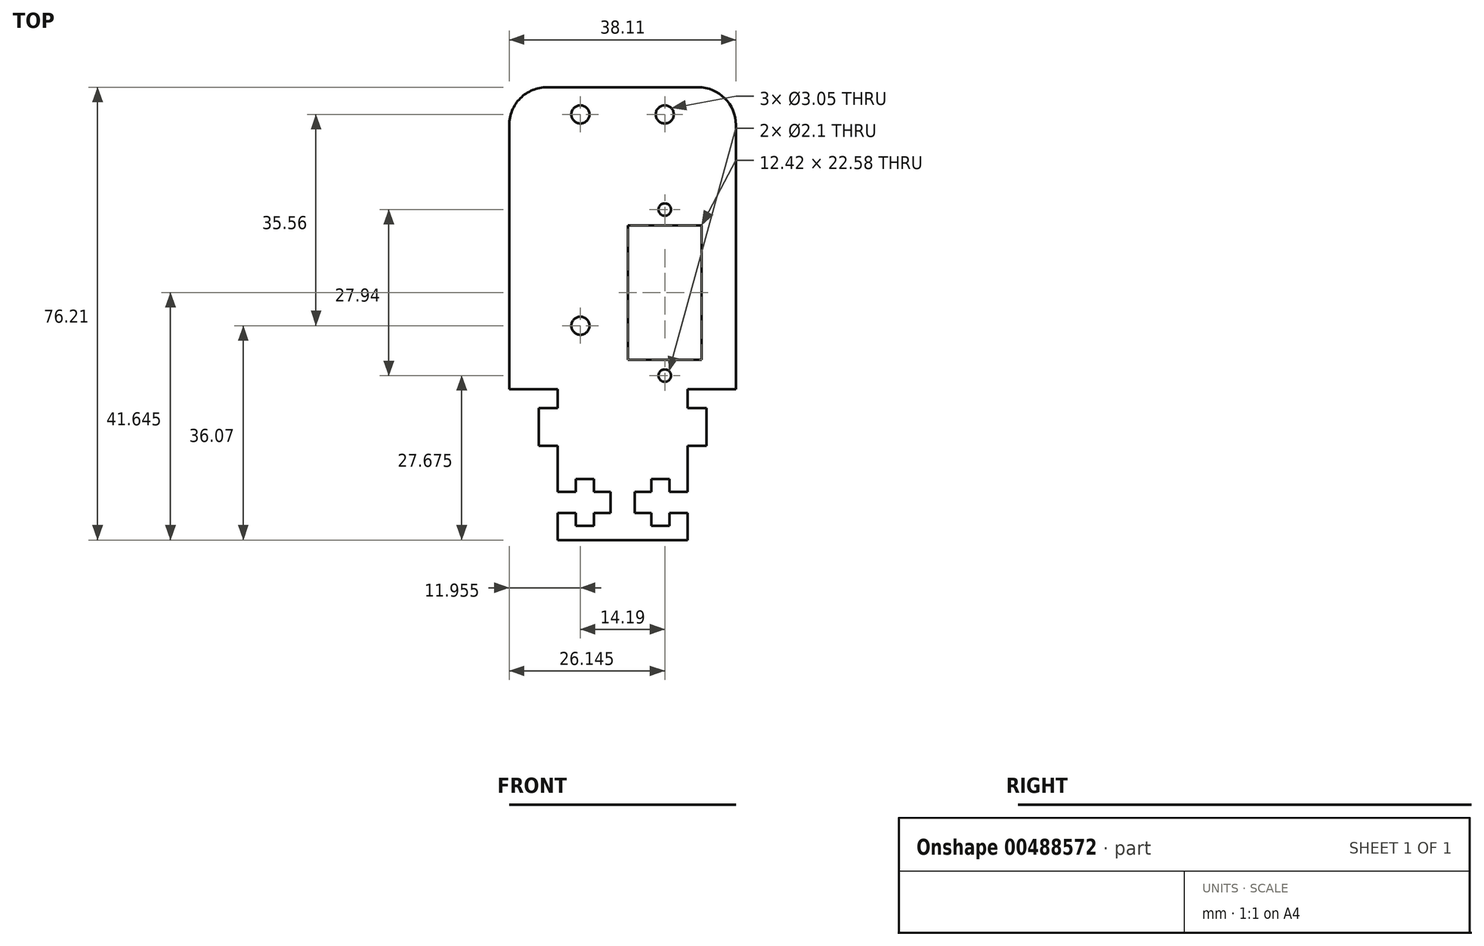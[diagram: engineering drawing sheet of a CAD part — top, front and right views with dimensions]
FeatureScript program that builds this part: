
annotation { "Feature Type Name" : "Feature", "Feature Type Description" : "" }
export const myFeature = defineFeature(function(context is Context, id is Id, definition is map)
    precondition{}
    {
        {
            var Q0;
            Q0=qCreatedBy(makeId("Top.planeOp"),FACE);
            var sketch = newSketch(context, id + "F0", { "sketchPlane" : qUnion([Q0])});
            skLineSegment(sketch, "E0.bottom", {"start": v(12.7, 41.7) * mm, "end": v(-12.7, 41.7) * mm});
            skLineSegment(sketch, "E0.left", {"start": v(19.05, 35.36) * mm, "end": v(19.06, -9.1) * mm});
            skLineSegment(sketch, "E0.right", {"start": v(-19.05, 35.35) * mm, "end": v(-19.04, -9.1) * mm});
            skPoint(sketch, "E0.middle", {"position": v(0, 0) * mm});
            skLineSegment(sketch, "E1.bottom", {"start": v(0.88, -4.14) * mm, "end": v(13.3, -4.14) * mm});
            skLineSegment(sketch, "E1.top", {"start": v(0.88, 18.44) * mm, "end": v(13.3, 18.44) * mm});
            skLineSegment(sketch, "E1.left", {"start": v(0.88, -4.14) * mm, "end": v(0.88, 18.44) * mm});
            skLineSegment(sketch, "E1.right", {"start": v(13.3, -4.14) * mm, "end": v(13.3, 18.44) * mm});
            skCircle(sketch, "E2", {"center": v(7.1, 1.57) * mm, "radius": 4.47 * mm, "construction": true});
            skPoint(sketch, "E2.centerSnap0", {"position": v(7.1, -4.14) * mm});
            skCircle(sketch, "E3", {"center": v(7.1, 6.04) * mm, "radius": 1.76 * mm, "construction": true});
            skCircle(sketch, "E4", {"center": v(-7.1, 1.57) * mm, "radius": 1.52 * mm});
            skLineSegment(sketch, "E5.bottom", {"start": v(13.3, 23.26) * mm, "end": v(1.1, 23.26) * mm, "construction": true});
            skLineSegment(sketch, "E5.top", {"start": v(13.3, -8.97) * mm, "end": v(1.1, -8.97) * mm, "construction": true});
            skLineSegment(sketch, "E5.left", {"start": v(13.3, 23.26) * mm, "end": v(13.3, -8.97) * mm, "construction": true});
            skLineSegment(sketch, "E5.right", {"start": v(1.1, 23.26) * mm, "end": v(1.1, -8.97) * mm, "construction": true});
            skPoint(sketch, "E5.middle.positionSnap0", {"position": v(0, 7.03) * mm});
            skPoint(sketch, "E5.middle.positionSnap1", {"position": v(7.1, 18.44) * mm});
            skPoint(sketch, "E5.centerSnap0", {"position": v(0.88, 7.15) * mm});
            skPoint(sketch, "E5.centerSnap1", {"position": v(7.1, 18.44) * mm});
            skCircle(sketch, "E6", {"center": v(7.1, 37.13) * mm, "radius": 1.52 * mm});
            skCircle(sketch, "E7", {"center": v(7.1, -6.82) * mm, "radius": 1.05 * mm});
            skCircle(sketch, "E8", {"center": v(-7.1, 37.13) * mm, "radius": 1.52 * mm});
            skPoint(sketch, "E9.visualSharp", {"position": v(-19.05, 41.7) * mm});
            skArc(sketch, "E9.filletArc", {"start": v(-12.7, 41.7) * mm, "mid": v(-17.2, 39.84) * mm, "end": v(-19.05, 35.35) * mm});
            skPoint(sketch, "E10.visualSharp", {"position": v(19.05, 41.7) * mm});
            skArc(sketch, "E10.filletArc", {"start": v(19.05, 35.36) * mm, "mid": v(17.19, 39.85) * mm, "end": v(12.7, 41.7) * mm});
            skCircle(sketch, "E11", {"center": v(7.1, 21.12) * mm, "radius": 1.05 * mm});
            skLineSegment(sketch, "E12", {"start": v(-7.1, 1.57) * mm, "end": v(0, 1.57) * mm, "construction": true});
            skLineSegment(sketch, "E13", {"start": v(0, 1.57) * mm, "end": v(7.1, 1.57) * mm, "construction": true});
            skLineSegment(sketch, "E14", {"start": v(-19.04, -9.1) * mm, "end": v(-10.9, -9.1) * mm});
            skLineSegment(sketch, "E15", {"start": v(-10.9, -9.1) * mm, "end": v(-10.9, -12.27) * mm});
            skLineSegment(sketch, "E16", {"start": v(-10.9, -34.5) * mm, "end": v(10.92, -34.5) * mm});
            skLineSegment(sketch, "E17", {"start": v(10.92, -34.5) * mm, "end": v(10.92, -29.93) * mm});
            skLineSegment(sketch, "E18", {"start": v(10.92, -9.1) * mm, "end": v(19.06, -9.1) * mm});
            skLineSegment(sketch, "E19.right", {"start": v(-14.07, -12.27) * mm, "end": v(-14.07, -18.62) * mm});
            skLineSegment(sketch, "E20", {"start": v(-14.07, -12.27) * mm, "end": v(-10.9, -12.27) * mm});
            skLineSegment(sketch, "E21", {"start": v(-14.07, -18.62) * mm, "end": v(-10.9, -18.62) * mm});
            skLineSegment(sketch, "E22", {"start": v(10.92, -12.27) * mm, "end": v(14.1, -12.27) * mm});
            skLineSegment(sketch, "E23", {"start": v(14.1, -12.27) * mm, "end": v(14.1, -18.62) * mm});
            skLineSegment(sketch, "E24", {"start": v(14.1, -18.62) * mm, "end": v(10.92, -18.62) * mm});
            skLineSegment(sketch, "E25.trimOffspring", {"start": v(10.92, -12.27) * mm, "end": v(10.92, -9.1) * mm});
            skLineSegment(sketch, "E26.trimOffspring", {"start": v(-10.9, -18.62) * mm, "end": v(-10.9, -26.37) * mm});
            skLineSegment(sketch, "E27.bottom", {"start": v(10.92, -26.37) * mm, "end": v(7.85, -26.37) * mm});
            skLineSegment(sketch, "E27.top", {"start": v(10.92, -29.93) * mm, "end": v(7.85, -29.93) * mm});
            skLineSegment(sketch, "E27.right", {"start": v(2.03, -26.37) * mm, "end": v(2.03, -29.93) * mm});
            skLineSegment(sketch, "E28.bottom", {"start": v(7.85, -32.08) * mm, "end": v(4.8, -32.08) * mm});
            skLineSegment(sketch, "E28.top", {"start": v(7.85, -24.21) * mm, "end": v(4.8, -24.21) * mm});
            skLineSegment(sketch, "E28.left", {"start": v(7.85, -32.08) * mm, "end": v(7.85, -29.93) * mm});
            skLineSegment(sketch, "E28.right", {"start": v(4.8, -32.08) * mm, "end": v(4.8, -29.93) * mm});
            skPoint(sketch, "E28.middle", {"position": v(6.33, -28.15) * mm});
            skPoint(sketch, "E28.middle.positionSnap0", {"position": v(10.92, -28.15) * mm});
            skPoint(sketch, "E28.centerSnap0", {"position": v(10.92, -28.15) * mm});
            skLineSegment(sketch, "E29.trimOffspring", {"start": v(4.8, -26.37) * mm, "end": v(2.03, -26.37) * mm});
            skLineSegment(sketch, "E30.trimOffspring", {"start": v(4.8, -26.37) * mm, "end": v(4.8, -24.21) * mm});
            skLineSegment(sketch, "E31.trimOffspring", {"start": v(7.85, -26.37) * mm, "end": v(7.85, -24.21) * mm});
            skLineSegment(sketch, "E32.trimOffspring", {"start": v(4.8, -29.93) * mm, "end": v(2.03, -29.93) * mm});
            skLineSegment(sketch, "E33.trimOffspring", {"start": v(10.92, -26.37) * mm, "end": v(10.92, -18.62) * mm});
            skLineSegment(sketch, "E34.MirrorCS", {"start": v(-10.92, -26.37) * mm, "end": v(-7.85, -26.37) * mm});
            skLineSegment(sketch, "E35.MirrorCS", {"start": v(-10.92, -29.93) * mm, "end": v(-7.85, -29.93) * mm});
            skLineSegment(sketch, "E36.MirrorCS", {"start": v(-7.85, -32.08) * mm, "end": v(-4.8, -32.08) * mm});
            skLineSegment(sketch, "E37.MirrorCS", {"start": v(-7.85, -32.08) * mm, "end": v(-7.85, -29.93) * mm});
            skLineSegment(sketch, "E38.MirrorCS", {"start": v(-4.8, -32.08) * mm, "end": v(-4.8, -29.93) * mm});
            skLineSegment(sketch, "E39.MirrorCS", {"start": v(-4.8, -29.93) * mm, "end": v(-2.03, -29.93) * mm});
            skLineSegment(sketch, "E40.MirrorCS", {"start": v(-2.03, -26.37) * mm, "end": v(-2.03, -29.93) * mm});
            skLineSegment(sketch, "E41.MirrorCS", {"start": v(-4.8, -26.37) * mm, "end": v(-2.03, -26.37) * mm});
            skLineSegment(sketch, "E42.MirrorCS", {"start": v(-4.8, -26.37) * mm, "end": v(-4.8, -24.21) * mm});
            skLineSegment(sketch, "E43.MirrorCS", {"start": v(-7.85, -24.21) * mm, "end": v(-4.8, -24.21) * mm});
            skLineSegment(sketch, "E44.MirrorCS", {"start": v(-7.85, -26.37) * mm, "end": v(-7.85, -24.21) * mm});
            skLineSegment(sketch, "E45.trimOffspring", {"start": v(-10.9, -29.93) * mm, "end": v(-10.9, -34.5) * mm});
            skLineSegment(sketch, "E46", {"start": v(7.1, 18.44) * mm, "end": v(7.1, 21.12) * mm, "construction": true});
            skLineSegment(sketch, "E47", {"start": v(7.1, -4.14) * mm, "end": v(7.1, -6.82) * mm, "construction": true});
            skSolve(sketch);
        }
        {
            var Q0;
            Q0=makeQuery(id+"F0.imprint","IMPRINT",FACE,{"disambiguationData":[TD([[makeQuery(id+"F0.imprint","IMPRINT",EDGE,{"derivedFrom":sQuery(id+"F0.wireOp",EDGE,"E0.bottom")}),1.0]])]});
            var Q1;
            {var subQ0=sQuery(id+"F0.wireOp",EDGE,"E22");Q1=makeQuery(id+"F0.imprint","IMPRINT",FACE,{"disambiguationData":[TD([[makeQuery(id+"F0.imprint","IMPRINT",EDGE,{"derivedFrom":subQ0}),-1.0]])]});}
            var Q2;
            Q2=makeQuery(id+"F0.imprint","IMPRINT",FACE,{"disambiguationData":[TD([[makeQuery(id+"F0.imprint","IMPRINT",EDGE,{"derivedFrom":sQuery(id+"F0.wireOp",EDGE,"E19.right")}),1.0]])]});
            extrude(context, id + "F1", {"entities" : qUnion([Q0, Q1, Q2]), "depth" : 1 / 203.2 * mm});
        }
    });
